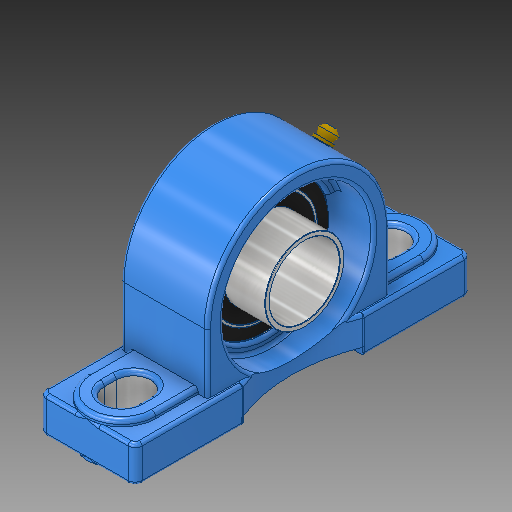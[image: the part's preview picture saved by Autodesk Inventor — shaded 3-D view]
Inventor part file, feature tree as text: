
AUTODESK INVENTOR PART (.ipt)
format: ipt  version: 2019 (Build 230136000, 136)  size: 681,472 bytes
history: native  units: in
note: dims shown in document units (in); Inventor stores cm internally (conversion verified against a paired STEP export)
features: sketch x28, plane x7, other x3
ambient origin geometry x8: Origin, YZ Plane, XZ Plane, XY Plane, X Axis, Y Axis, Z Axis, Center Point
bodies: Solid1 (feature_tree)
feature tree (38):
  other  "Pillow Bearing inventor_MIR.ipt"
  other  "Solid1::Pillow Bearing inventor_MIR.ipt"
  other  "TaggingFeature1"
  sketch  "Sketch1"  dims[d0=0.3937in]
  sketch  "Sketch2"
  sketch  "Sketch3"
  sketch  "Sketch4"
  sketch  "Sketch5"
  sketch  "Sketch6"
  sketch  "Sketch7"
  sketch  "Sketch8"
  sketch  "Sketch9"
  sketch  "Sketch10"
  sketch  "Sketch11"
  sketch  "Sketch13"
  sketch  "Sketch14"
  sketch  "Sketch15"
  sketch  "Sketch17"
  sketch  "Sketch18"
  sketch  "Sketch19"
  sketch  "Sketch20"
  sketch  "Sketch21"
  sketch  "Sketch22"
  sketch  "Sketch23"
  sketch  "Sketch24"
  sketch  "Sketch25"
  sketch  "Sketch26"
  sketch  "Sketch27"
  sketch  "Sketch28"
  sketch  "Sketch29"
  sketch  "Sketch30"
  plane  "Work Plane1"
  plane  "Work Plane2"
  plane  "Work Plane5"
  plane  "Work Plane6"
  plane  "Work Plane7"
  plane  "Work Plane8"
  plane  "Work Plane9"
